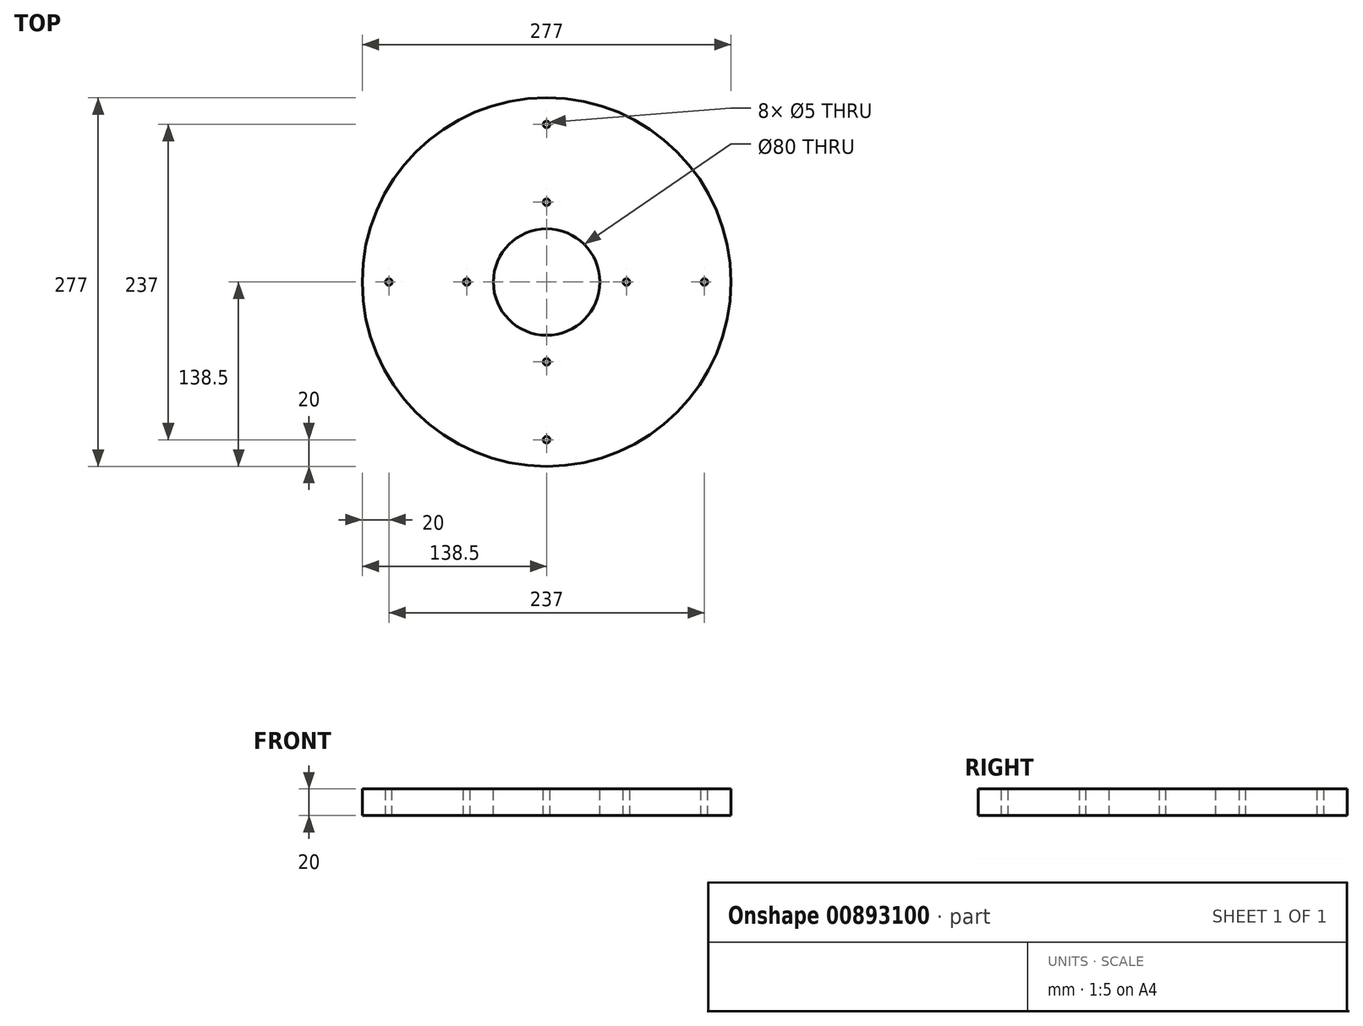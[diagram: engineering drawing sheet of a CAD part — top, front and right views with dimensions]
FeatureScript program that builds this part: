
annotation { "Feature Type Name" : "Feature", "Feature Type Description" : "" }
export const myFeature = defineFeature(function(context is Context, id is Id, definition is map)
    precondition{}
    {
        {
            var Q0;
            Q0=qCreatedBy(makeId("Top.planeOp"),FACE);
            var sketch = newSketch(context, id + "F0", { "sketchPlane" : qUnion([Q0])});
            skCircle(sketch, "E0", {"center": v(0, 0) * mm, "radius": 138.5 * mm});
            skSolve(sketch);
        }
        {
            var Q0;
            Q0=makeQuery(id+"F0.imprint","IMPRINT",FACE,{"disambiguationData":[TD([[makeQuery(id+"F0.imprint","IMPRINT",EDGE,{"derivedFrom":sQuery(id+"F0.wireOp",EDGE,"E0")}),1.0]])]});
            extrude(context, id + "F1", {"entities" : qUnion([Q0]), "depth" : 20 * mm, "offsetDistance" : 25 * mm});
        }
        {
            var Q0;
            Q0=makeQuery(id+"F1.opExtrude","CAP_FACE",FACE,{"disambiguationData":[OSD([sQuery(id+"F0.wireOp",EDGE,"E0")])],"isStart":false});
            var sketch = newSketch(context, id + "F2", { "sketchPlane" : qUnion([Q0])});
            skCircle(sketch, "E1", {"center": v(0, 0) * mm, "radius": 40 * mm});
            skSolve(sketch);
        }
        {
            var Q0;
            Q0=makeQuery(id+"F2.imprint","IMPRINT",FACE,{"disambiguationData":[TD([[makeQuery(id+"F2.imprint","IMPRINT",EDGE,{"derivedFrom":sQuery(id+"F2.wireOp",EDGE,"E1")}),1.0]])]});
            extrude(context, id + "F3", {"entities" : qUnion([Q0]), "operationType" : NewBodyOperationType.REMOVE, "oppositeDirection" : true, "depth" : 25 * mm, "offsetDistance" : 25 * mm});
        }
        {
            var Q0;
            Q0=makeQuery(id+"F1.opExtrude","CAP_FACE",FACE,{"disambiguationData":[OSD([sQuery(id+"F0.wireOp",EDGE,"E0")])],"isStart":false});
            var sketch = newSketch(context, id + "F4", { "sketchPlane" : qUnion([Q0])});
            skCircle(sketch, "E2", {"center": v(0, 0) * mm, "radius": 60 * mm});
            skCircle(sketch, "E3", {"center": v(0, 60) * mm, "radius": 2.5 * mm});
            skCircle(sketch, "E4", {"center": v(60, 0) * mm, "radius": 2.5 * mm});
            skCircle(sketch, "E5", {"center": v(0, -60) * mm, "radius": 2.5 * mm});
            skCircle(sketch, "E6", {"center": v(-60, 0) * mm, "radius": 2.5 * mm});
            skSolve(sketch);
        }
        {
            var Q0;
            {var subQ0=sQuery(id+"F4.wireOp",EDGE,"E3");var subQ1=sQuery(id+"F4.wireOp",EDGE,"E2");var subQ2=makeQuery(id+"F4.imprint","INTERSECT",VERTEX,{"disambiguationData":[OD(0.0)],"derivedFrom":[subQ1,subQ0]});Q0=makeQuery(id+"F4.imprint","IMPRINT",FACE,{"disambiguationData":[TD([[makeQuery(id+"F4.imprint","IMPRINT",EDGE,{"disambiguationData":[TD([[subQ2,-1.0]])],"derivedFrom":subQ1}),-1.0]])]});}
            var Q1;
            {var subQ0=sQuery(id+"F4.wireOp",EDGE,"E3");var subQ1=sQuery(id+"F4.wireOp",EDGE,"E2");var subQ2=makeQuery(id+"F4.imprint","INTERSECT",VERTEX,{"disambiguationData":[OD(0.0)],"derivedFrom":[subQ1,subQ0]});Q1=makeQuery(id+"F4.imprint","IMPRINT",FACE,{"disambiguationData":[TD([[makeQuery(id+"F4.imprint","IMPRINT",EDGE,{"disambiguationData":[TD([[subQ2,-1.0]])],"derivedFrom":subQ1}),1.0]])]});}
            var Q2;
            {var subQ0=sQuery(id+"F4.wireOp",EDGE,"E6");var subQ1=sQuery(id+"F4.wireOp",EDGE,"E2");var subQ2=makeQuery(id+"F4.imprint","INTERSECT",VERTEX,{"disambiguationData":[OD(0.0)],"derivedFrom":[subQ1,subQ0]});Q2=makeQuery(id+"F4.imprint","IMPRINT",FACE,{"disambiguationData":[TD([[makeQuery(id+"F4.imprint","IMPRINT",EDGE,{"disambiguationData":[TD([[subQ2,-1.0]])],"derivedFrom":subQ1}),1.0]])]});}
            var Q3;
            {var subQ0=sQuery(id+"F4.wireOp",EDGE,"E6");var subQ1=sQuery(id+"F4.wireOp",EDGE,"E2");var subQ2=makeQuery(id+"F4.imprint","INTERSECT",VERTEX,{"disambiguationData":[OD(0.0)],"derivedFrom":[subQ1,subQ0]});Q3=makeQuery(id+"F4.imprint","IMPRINT",FACE,{"disambiguationData":[TD([[makeQuery(id+"F4.imprint","IMPRINT",EDGE,{"disambiguationData":[TD([[subQ2,-1.0]])],"derivedFrom":subQ1}),-1.0]])]});}
            var Q4;
            {var subQ0=sQuery(id+"F4.wireOp",EDGE,"E4");var subQ1=sQuery(id+"F4.wireOp",EDGE,"E2");var subQ2=makeQuery(id+"F4.imprint","INTERSECT",VERTEX,{"disambiguationData":[OD(0.0)],"derivedFrom":[subQ1,subQ0]});Q4=makeQuery(id+"F4.imprint","IMPRINT",FACE,{"disambiguationData":[TD([[makeQuery(id+"F4.imprint","IMPRINT",EDGE,{"disambiguationData":[TD([[subQ2,1.0]])],"derivedFrom":subQ1}),-1.0]])]});}
            var Q5;
            {var subQ0=sQuery(id+"F4.wireOp",EDGE,"E4");var subQ1=sQuery(id+"F4.wireOp",EDGE,"E2");var subQ2=makeQuery(id+"F4.imprint","INTERSECT",VERTEX,{"disambiguationData":[OD(0.0)],"derivedFrom":[subQ1,subQ0]});Q5=makeQuery(id+"F4.imprint","IMPRINT",FACE,{"disambiguationData":[TD([[makeQuery(id+"F4.imprint","IMPRINT",EDGE,{"disambiguationData":[TD([[subQ2,1.0]])],"derivedFrom":subQ1}),1.0]])]});}
            var Q6;
            {var subQ0=sQuery(id+"F4.wireOp",EDGE,"E5");var subQ1=sQuery(id+"F4.wireOp",EDGE,"E2");var subQ2=makeQuery(id+"F4.imprint","INTERSECT",VERTEX,{"disambiguationData":[OD(0.0)],"derivedFrom":[subQ1,subQ0]});Q6=makeQuery(id+"F4.imprint","IMPRINT",FACE,{"disambiguationData":[TD([[makeQuery(id+"F4.imprint","IMPRINT",EDGE,{"disambiguationData":[TD([[subQ2,-1.0]])],"derivedFrom":subQ1}),-1.0]])]});}
            var Q7;
            {var subQ0=sQuery(id+"F4.wireOp",EDGE,"E5");var subQ1=sQuery(id+"F4.wireOp",EDGE,"E2");var subQ2=makeQuery(id+"F4.imprint","INTERSECT",VERTEX,{"disambiguationData":[OD(0.0)],"derivedFrom":[subQ1,subQ0]});Q7=makeQuery(id+"F4.imprint","IMPRINT",FACE,{"disambiguationData":[TD([[makeQuery(id+"F4.imprint","IMPRINT",EDGE,{"disambiguationData":[TD([[subQ2,-1.0]])],"derivedFrom":subQ1}),1.0]])]});}
            extrude(context, id + "F5", {"entities" : qUnion([Q0, Q1, Q2, Q3, Q4, Q5, Q6, Q7]), "operationType" : NewBodyOperationType.REMOVE, "oppositeDirection" : true, "depth" : 25 * mm, "offsetDistance" : 25 * mm});
        }
        {
            var Q0;
            Q0=makeQuery(id+"F1.opExtrude","CAP_FACE",FACE,{"disambiguationData":[OSD([sQuery(id+"F0.wireOp",EDGE,"E0")])],"isStart":false});
            var sketch = newSketch(context, id + "F6", { "sketchPlane" : qUnion([Q0])});
            skCircle(sketch, "E7", {"center": v(0, 0) * mm, "radius": 118.5 * mm});
            skCircle(sketch, "E8", {"center": v(0, 118.5) * mm, "radius": 2.5 * mm});
            skCircle(sketch, "E9", {"center": v(118.5, 0) * mm, "radius": 2.5 * mm});
            skCircle(sketch, "E10", {"center": v(0, -118.5) * mm, "radius": 2.5 * mm});
            skCircle(sketch, "E11", {"center": v(-118.5, 0) * mm, "radius": 2.5 * mm});
            skSolve(sketch);
        }
        {
            var Q0;
            {var subQ0=sQuery(id+"F6.wireOp",EDGE,"E8");var subQ1=sQuery(id+"F6.wireOp",EDGE,"E7");var subQ2=makeQuery(id+"F6.imprint","INTERSECT",VERTEX,{"disambiguationData":[OD(0.0)],"derivedFrom":[subQ1,subQ0]});Q0=makeQuery(id+"F6.imprint","IMPRINT",FACE,{"disambiguationData":[TD([[makeQuery(id+"F6.imprint","IMPRINT",EDGE,{"disambiguationData":[TD([[subQ2,-1.0]])],"derivedFrom":subQ1}),-1.0]])]});}
            var Q1;
            {var subQ0=sQuery(id+"F6.wireOp",EDGE,"E8");var subQ1=sQuery(id+"F6.wireOp",EDGE,"E7");var subQ2=makeQuery(id+"F6.imprint","INTERSECT",VERTEX,{"disambiguationData":[OD(0.0)],"derivedFrom":[subQ1,subQ0]});Q1=makeQuery(id+"F6.imprint","IMPRINT",FACE,{"disambiguationData":[TD([[makeQuery(id+"F6.imprint","IMPRINT",EDGE,{"disambiguationData":[TD([[subQ2,-1.0]])],"derivedFrom":subQ1}),1.0]])]});}
            var Q2;
            {var subQ0=sQuery(id+"F6.wireOp",EDGE,"E11");var subQ1=sQuery(id+"F6.wireOp",EDGE,"E7");var subQ2=makeQuery(id+"F6.imprint","INTERSECT",VERTEX,{"disambiguationData":[OD(0.0)],"derivedFrom":[subQ1,subQ0]});Q2=makeQuery(id+"F6.imprint","IMPRINT",FACE,{"disambiguationData":[TD([[makeQuery(id+"F6.imprint","IMPRINT",EDGE,{"disambiguationData":[TD([[subQ2,-1.0]])],"derivedFrom":subQ1}),1.0]])]});}
            var Q3;
            {var subQ0=sQuery(id+"F6.wireOp",EDGE,"E11");var subQ1=sQuery(id+"F6.wireOp",EDGE,"E7");var subQ2=makeQuery(id+"F6.imprint","INTERSECT",VERTEX,{"disambiguationData":[OD(0.0)],"derivedFrom":[subQ1,subQ0]});Q3=makeQuery(id+"F6.imprint","IMPRINT",FACE,{"disambiguationData":[TD([[makeQuery(id+"F6.imprint","IMPRINT",EDGE,{"disambiguationData":[TD([[subQ2,-1.0]])],"derivedFrom":subQ1}),-1.0]])]});}
            var Q4;
            {var subQ0=sQuery(id+"F6.wireOp",EDGE,"E10");var subQ1=sQuery(id+"F6.wireOp",EDGE,"E7");var subQ2=makeQuery(id+"F6.imprint","INTERSECT",VERTEX,{"disambiguationData":[OD(0.0)],"derivedFrom":[subQ1,subQ0]});Q4=makeQuery(id+"F6.imprint","IMPRINT",FACE,{"disambiguationData":[TD([[makeQuery(id+"F6.imprint","IMPRINT",EDGE,{"disambiguationData":[TD([[subQ2,-1.0]])],"derivedFrom":subQ1}),1.0]])]});}
            var Q5;
            {var subQ0=sQuery(id+"F6.wireOp",EDGE,"E10");var subQ1=sQuery(id+"F6.wireOp",EDGE,"E7");var subQ2=makeQuery(id+"F6.imprint","INTERSECT",VERTEX,{"disambiguationData":[OD(0.0)],"derivedFrom":[subQ1,subQ0]});Q5=makeQuery(id+"F6.imprint","IMPRINT",FACE,{"disambiguationData":[TD([[makeQuery(id+"F6.imprint","IMPRINT",EDGE,{"disambiguationData":[TD([[subQ2,-1.0]])],"derivedFrom":subQ1}),-1.0]])]});}
            var Q6;
            {var subQ0=sQuery(id+"F6.wireOp",EDGE,"E9");var subQ1=sQuery(id+"F6.wireOp",EDGE,"E7");var subQ2=makeQuery(id+"F6.imprint","INTERSECT",VERTEX,{"disambiguationData":[OD(0.0)],"derivedFrom":[subQ1,subQ0]});Q6=makeQuery(id+"F6.imprint","IMPRINT",FACE,{"disambiguationData":[TD([[makeQuery(id+"F6.imprint","IMPRINT",EDGE,{"disambiguationData":[TD([[subQ2,1.0]])],"derivedFrom":subQ1}),1.0]])]});}
            var Q7;
            {var subQ0=sQuery(id+"F6.wireOp",EDGE,"E9");var subQ1=sQuery(id+"F6.wireOp",EDGE,"E7");var subQ2=makeQuery(id+"F6.imprint","INTERSECT",VERTEX,{"disambiguationData":[OD(0.0)],"derivedFrom":[subQ1,subQ0]});Q7=makeQuery(id+"F6.imprint","IMPRINT",FACE,{"disambiguationData":[TD([[makeQuery(id+"F6.imprint","IMPRINT",EDGE,{"disambiguationData":[TD([[subQ2,1.0]])],"derivedFrom":subQ1}),-1.0]])]});}
            extrude(context, id + "F7", {"entities" : qUnion([Q0, Q1, Q2, Q3, Q4, Q5, Q6, Q7]), "operationType" : NewBodyOperationType.REMOVE, "endBound" : BoundingType.THROUGH_ALL, "oppositeDirection" : true, "depth" : 25 * mm, "offsetDistance" : 25 * mm});
        }
    });
